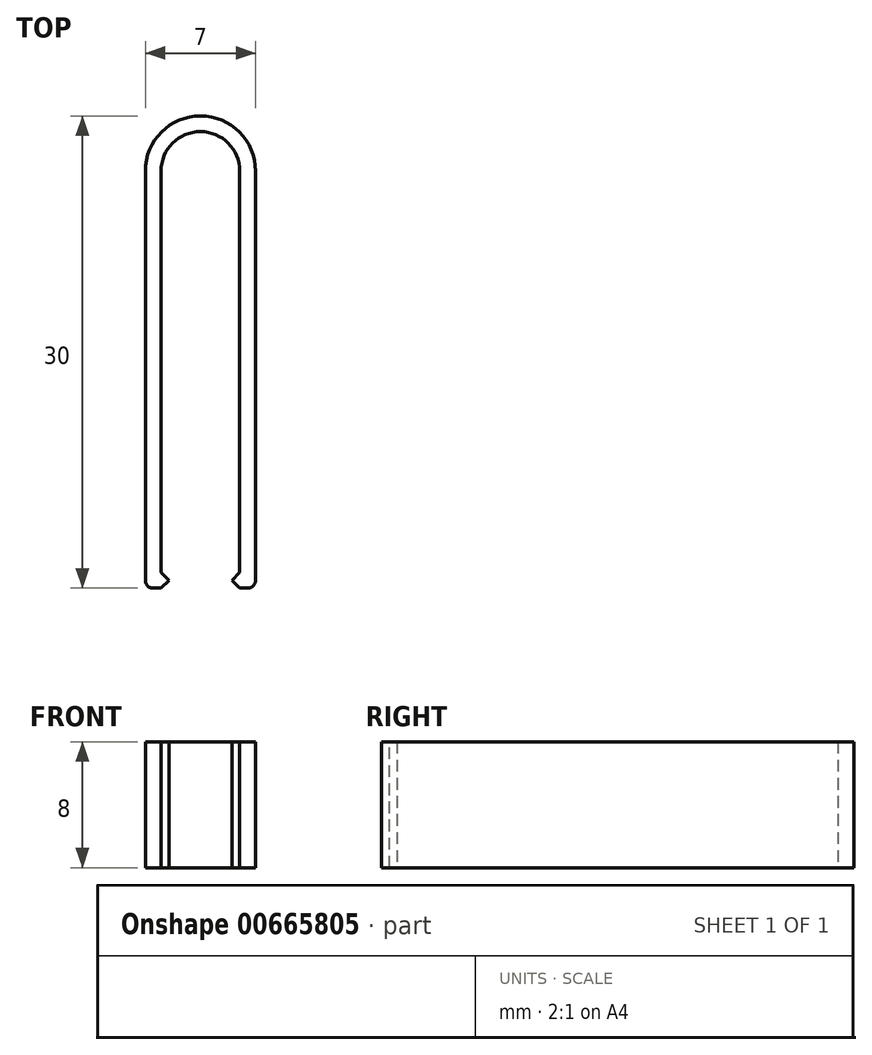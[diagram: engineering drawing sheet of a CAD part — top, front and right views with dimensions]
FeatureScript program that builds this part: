
annotation { "Feature Type Name" : "Feature", "Feature Type Description" : "" }
export const myFeature = defineFeature(function(context is Context, id is Id, definition is map)
    precondition{}
    {
        {
            var Q0;
            Q0=qCreatedBy(makeId("Top.planeOp"),FACE);
            var sketch = newSketch(context, id + "F0", { "sketchPlane" : qUnion([Q0])});
            skLineSegment(sketch, "E0.left", {"start": v(-2.5, 12.75) * mm, "end": v(-2.5, -12.75) * mm});
            skPoint(sketch, "E0.middle", {"position": v(-3, 0) * mm});
            skArc(sketch, "E1", {"start": v(0, 15.25) * mm, "mid": v(-1.77, 14.52) * mm, "end": v(-2.5, 12.75) * mm});
            skLineSegment(sketch, "E2.MirrorCS", {"start": v(2.5, 12.75) * mm, "end": v(2.5, -12.75) * mm});
            skArc(sketch, "E3.MirrorCS", {"start": v(0, 15.25) * mm, "mid": v(1.77, 14.52) * mm, "end": v(2.5, 12.75) * mm});
            skArc(sketch, "E4", {"start": v(0, 16.25) * mm, "mid": v(-2.47, 15.22) * mm, "end": v(-3.5, 12.75) * mm});
            skArc(sketch, "E5.MirrorCS", {"start": v(0, 16.25) * mm, "mid": v(2.47, 15.22) * mm, "end": v(3.5, 12.75) * mm});
            skLineSegment(sketch, "E6.top", {"start": v(-3.5, -13.75) * mm, "end": v(-2, -13.75) * mm});
            skLineSegment(sketch, "E6.right", {"start": v(-2, -12.75) * mm, "end": v(-2, -13.75) * mm});
            skLineSegment(sketch, "E7", {"start": v(-2.5, -12.75) * mm, "end": v(-2, -12.75) * mm});
            skLineSegment(sketch, "E8.MirrorCS", {"start": v(2, -12.75) * mm, "end": v(2, -13.75) * mm});
            skLineSegment(sketch, "E9.MirrorCS", {"start": v(2.5, -12.75) * mm, "end": v(2, -12.75) * mm});
            skLineSegment(sketch, "E10.MirrorCS", {"start": v(3.5, -13.75) * mm, "end": v(2, -13.75) * mm});
            skLineSegment(sketch, "E11", {"start": v(-3.5, 12.75) * mm, "end": v(-3.5, -13.75) * mm});
            skLineSegment(sketch, "E12.MirrorCS", {"start": v(3.5, 12.75) * mm, "end": v(3.5, -13.75) * mm});
            skSolve(sketch);
        }
        {
            var Q0;
            Q0=makeQuery(id+"F0.imprint","IMPRINT",FACE,{"disambiguationData":[TD([[makeQuery(id+"F0.imprint","IMPRINT",EDGE,{"derivedFrom":sQuery(id+"F0.wireOp",EDGE,"E0.left")}),-1.0]])]});
            extrude(context, id + "F1", {"entities" : qUnion([Q0]), "depth" : 8 * mm, "offsetDistance" : 25 * mm});
        }
        {
            var Q0;
            Q0=makeQuery(id+"F1.opExtrude","SWEPT_EDGE",EDGE,{"disambiguationData":[OSD([sQuery(id+"F0.wireOp",EDGE,"E6.top"),sQuery(id+"F0.wireOp",EDGE,"E11")])]});
            var Q1;
            Q1=makeQuery(id+"F1.opExtrude","SWEPT_EDGE",EDGE,{"disambiguationData":[OSD([sQuery(id+"F0.wireOp",EDGE,"E10.MirrorCS"),sQuery(id+"F0.wireOp",EDGE,"E12.MirrorCS")])]});
            fillet(context, id + "F2", {"entities" : qUnion([Q0, Q1]), "radius" : .5 * mm, "tangentPropagation" : true, "allowEdgeOverflow" : false});
        }
        {
            var Q0;
            Q0=makeQuery(id+"F1.opExtrude","SWEPT_EDGE",EDGE,{"disambiguationData":[OSD([sQuery(id+"F0.wireOp",EDGE,"E6.top"),sQuery(id+"F0.wireOp",EDGE,"E6.right")])]});
            var Q1;
            Q1=makeQuery(id+"F1.opExtrude","SWEPT_EDGE",EDGE,{"disambiguationData":[OSD([sQuery(id+"F0.wireOp",EDGE,"E6.right"),sQuery(id+"F0.wireOp",EDGE,"E7")])]});
            var Q2;
            Q2=makeQuery(id+"F1.opExtrude","SWEPT_EDGE",EDGE,{"disambiguationData":[OSD([sQuery(id+"F0.wireOp",EDGE,"E8.MirrorCS"),sQuery(id+"F0.wireOp",EDGE,"E10.MirrorCS")])]});
            var Q3;
            Q3=makeQuery(id+"F1.opExtrude","SWEPT_EDGE",EDGE,{"disambiguationData":[OSD([sQuery(id+"F0.wireOp",EDGE,"E8.MirrorCS"),sQuery(id+"F0.wireOp",EDGE,"E9.MirrorCS")])]});
            chamfer(context, id + "F3", {"entities" : qUnion([Q0, Q1, Q2, Q3]), "width" : .5 * mm, "tangentPropagation" : true});
        }
    });
